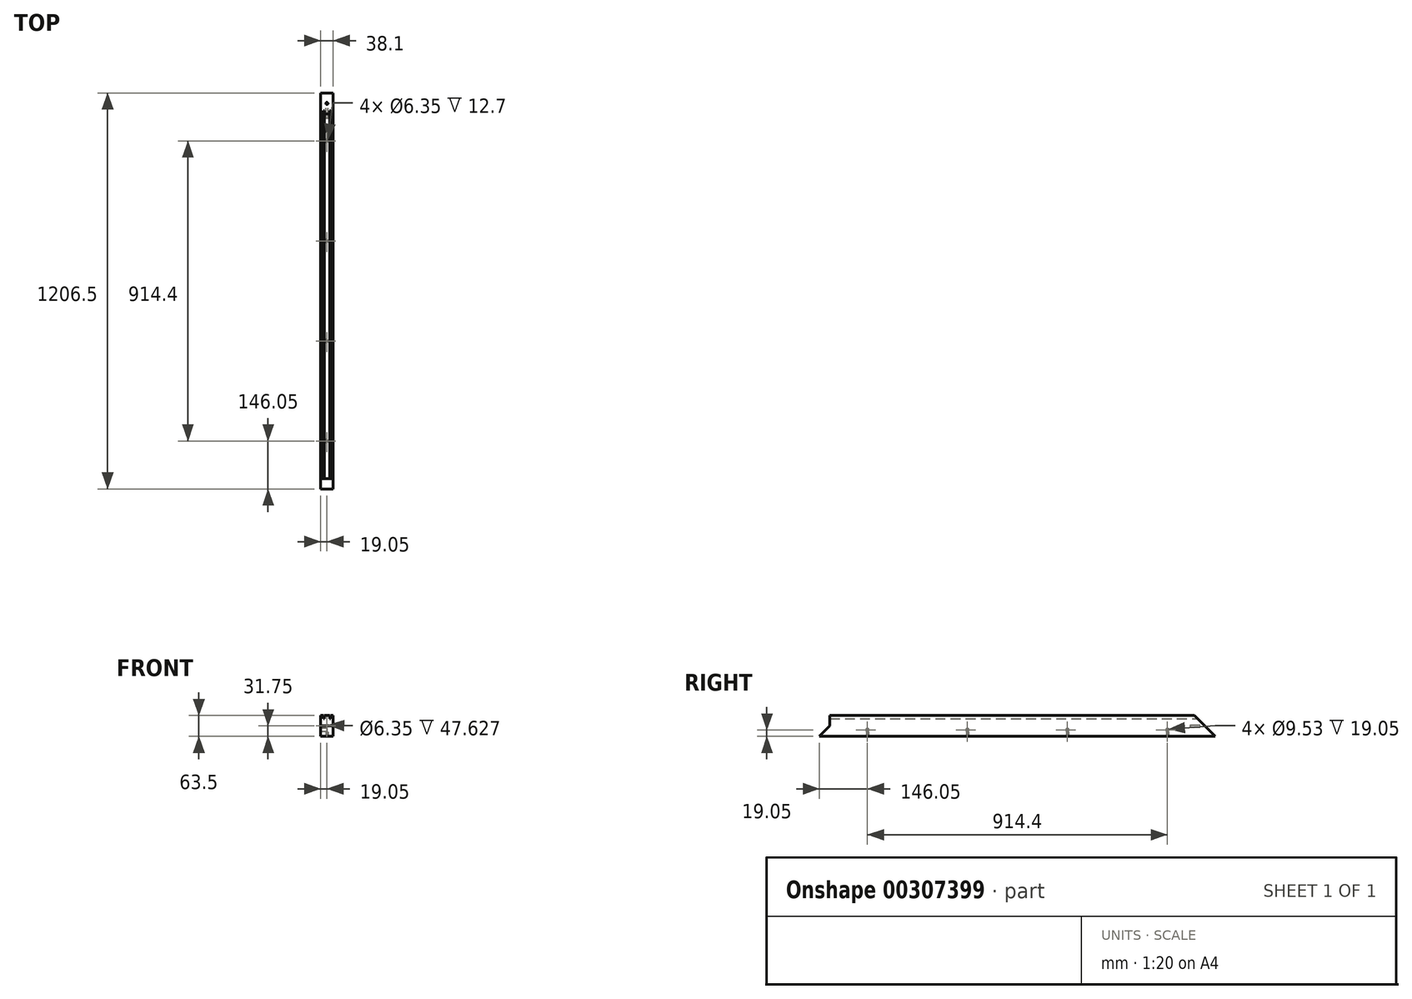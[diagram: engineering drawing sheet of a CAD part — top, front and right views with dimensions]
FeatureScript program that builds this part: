
annotation { "Feature Type Name" : "Feature", "Feature Type Description" : "" }
export const myFeature = defineFeature(function(context is Context, id is Id, definition is map)
    precondition{}
    {
        {
            var Q0;
            Q0=qCreatedBy(makeId("Front.planeOp"),FACE);
            var sketch = newSketch(context, id + "F0", { "sketchPlane" : qUnion([Q0])});
            skLineSegment(sketch, "E0.bottom", {"start": v(19.05, -31.75) * mm, "end": v(-19.05, -31.75) * mm});
            skLineSegment(sketch, "E0.top", {"start": v(19.05, 31.75) * mm, "end": v(-19.05, 31.75) * mm});
            skLineSegment(sketch, "E0.left", {"start": v(19.05, -31.75) * mm, "end": v(19.05, 31.75) * mm});
            skLineSegment(sketch, "E0.right", {"start": v(-19.05, -31.75) * mm, "end": v(-19.05, 31.75) * mm});
            skPoint(sketch, "E0.middle", {"position": v(0, 0) * mm});
            skLineSegment(sketch, "E1.bottom", {"start": v(11.11, 21.59) * mm, "end": v(7.94, 21.59) * mm});
            skLineSegment(sketch, "E1.top", {"start": v(11.11, 31.75) * mm, "end": v(7.94, 31.75) * mm});
            skLineSegment(sketch, "E1.left", {"start": v(11.11, 21.59) * mm, "end": v(11.11, 31.75) * mm});
            skLineSegment(sketch, "E1.right", {"start": v(7.94, 21.59) * mm, "end": v(7.94, 31.75) * mm});
            skPoint(sketch, "E1.middle", {"position": v(9.53, 26.67) * mm});
            skLineSegment(sketch, "E2.bottom", {"start": v(-7.94, 21.59) * mm, "end": v(-11.11, 21.59) * mm});
            skLineSegment(sketch, "E2.top", {"start": v(-7.94, 31.75) * mm, "end": v(-11.11, 31.75) * mm});
            skLineSegment(sketch, "E2.left", {"start": v(-7.94, 21.59) * mm, "end": v(-7.94, 31.75) * mm});
            skLineSegment(sketch, "E2.right", {"start": v(-11.11, 21.59) * mm, "end": v(-11.11, 31.75) * mm});
            skPoint(sketch, "E2.middle", {"position": v(-9.53, 26.67) * mm});
            skSolve(sketch);
        }
        {
            var Q0;
            Q0=makeQuery(id+"F0.imprint","IMPRINT",FACE,{"disambiguationData":[TD([[makeQuery(id+"F0.imprint","IMPRINT",EDGE,{"derivedFrom":sQuery(id+"F0.wireOp",EDGE,"E0.bottom")}),-1.0]])]});
            extrude(context, id + "F1", {"entities" : qUnion([Q0]), "endBound" : BoundingType.SYMMETRIC, "depth" : 1206.5 * mm});
        }
        {
            var Q0;
            Q0=qCreatedBy(makeId("Right.planeOp"),FACE);
            var sketch = newSketch(context, id + "F2", { "sketchPlane" : qUnion([Q0])});
            skLineSegment(sketch, "E3.MirrorCS", {"start": v(-571.5, 0) * mm, "end": v(-603.25, -31.75) * mm});
            skLineSegment(sketch, "E4.MirrorCS", {"start": v(-603.25, -31.75) * mm, "end": v(-603.25, 0) * mm});
            skLineSegment(sketch, "E5.MirrorCS", {"start": v(-571.5, 31.75) * mm, "end": v(-571.5, 0) * mm});
            skLineSegment(sketch, "E6.MirrorCS", {"start": v(-603.25, 31.75) * mm, "end": v(-603.25, 0) * mm});
            skLineSegment(sketch, "E7.MirrorCS", {"start": v(-603.25, 0) * mm, "end": v(-571.5, 0) * mm});
            skLineSegment(sketch, "E8.MirrorCS", {"start": v(-603.25, 31.75) * mm, "end": v(-571.5, 31.75) * mm});
            skPoint(sketch, "E9.MirrorP", {"position": v(-598.49, 4.76) * mm});
            skLineSegment(sketch, "E10", {"start": v(-571.5, 0) * mm, "end": v(-571.5, -31.75) * mm, "construction": true});
            skSolve(sketch);
        }
        {
            var Q0;
            Q0 = qSketchRegion(id + "F2", true);
            extrude(context, id + "F3", {"entities" : qUnion([Q0]), "operationType" : NewBodyOperationType.REMOVE, "endBound" : BoundingType.SYMMETRIC, "depth" : 127 * mm});
        }
        {
            var Q0;
            Q0=makeQuery(id+"F1.opExtrude","SWEPT_FACE",FACE,{"disambiguationData":[OSD([sQuery(id+"F0.wireOp",EDGE,"E0.right")])]});
            var sketch = newSketch(context, id + "F4", { "sketchPlane" : qUnion([Q0])});
            skLineSegment(sketch, "E11", {"start": v(-603.25, -31.75) * mm, "end": v(-539.75, 31.75) * mm});
            skLineSegment(sketch, "E12", {"start": v(-603.25, -31.75) * mm, "end": v(-603.25, 31.75) * mm});
            skLineSegment(sketch, "E13", {"start": v(-603.25, 31.75) * mm, "end": v(-539.75, 31.75) * mm});
            skSolve(sketch);
        }
        {
            var Q0;
            Q0=makeQuery(id+"F1.opExtrude","CAP_FACE",FACE,{"disambiguationData":[OSD([sQuery(id+"F0.wireOp",EDGE,"E0.bottom"),sQuery(id+"F0.wireOp",EDGE,"E0.top"),sQuery(id+"F0.wireOp",EDGE,"E0.left"),sQuery(id+"F0.wireOp",EDGE,"E0.right"),sQuery(id+"F0.wireOp",EDGE,"E1.bottom"),sQuery(id+"F0.wireOp",EDGE,"E1.left"),sQuery(id+"F0.wireOp",EDGE,"E1.right"),sQuery(id+"F0.wireOp",EDGE,"E2.bottom"),sQuery(id+"F0.wireOp",EDGE,"E2.left"),sQuery(id+"F0.wireOp",EDGE,"E2.right")])],"isStart":true});
            var sketch = newSketch(context, id + "F5", { "sketchPlane" : qUnion([Q0])});
            skCircle(sketch, "E14", {"center": v(0, 0) * mm, "radius": 3.18 * mm});
            skSolve(sketch);
        }
        {
            var Q0;
            Q0 = qSketchRegion(id + "F5", true);
            extrude(context, id + "F6", {"entities" : qUnion([Q0]), "operationType" : NewBodyOperationType.REMOVE, "oppositeDirection" : true, "depth" : 76.2 * mm});
        }
        {
            var Q0;
            Q0 = qSketchRegion(id + "F4", true);
            extrude(context, id + "F7", {"entities" : qUnion([Q0]), "operationType" : NewBodyOperationType.REMOVE, "oppositeDirection" : true, "depth" : 50.8 * mm});
        }
        {
            var Q0;
            Q0=makeQuery(id+"F1.opExtrude","SWEPT_FACE",FACE,{"disambiguationData":[OSD([sQuery(id+"F0.wireOp",EDGE,"E0.right")])]});
            var sketch = newSketch(context, id + "F8", { "sketchPlane" : qUnion([Q0])});
            skLineSegment(sketch, "E15.bottom", {"start": v(-603.25, -31.75) * mm, "end": v(603.25, -31.75) * mm, "construction": true});
            skLineSegment(sketch, "E15.top", {"start": v(-603.25, 6.35) * mm, "end": v(603.25, 6.35) * mm, "construction": true});
            skLineSegment(sketch, "E15.left", {"start": v(-603.25, -31.75) * mm, "end": v(-603.25, 6.35) * mm, "construction": true});
            skLineSegment(sketch, "E15.right", {"start": v(603.25, -31.75) * mm, "end": v(603.25, 6.35) * mm, "construction": true});
            skLineSegment(sketch, "E16", {"start": v(-603.25, -12.7) * mm, "end": v(603.25, -12.7) * mm, "construction": true});
            skPoint(sketch, "E17", {"position": v(0, -12.7) * mm});
            skPoint(sketch, "E18", {"position": v(-457.2, -12.7) * mm});
            skPoint(sketch, "E19", {"position": v(-152.4, -12.7) * mm});
            skPoint(sketch, "E20", {"position": v(152.4, -12.7) * mm});
            skPoint(sketch, "E21", {"position": v(457.2, -12.7) * mm});
            skLineSegment(sketch, "E22", {"start": v(0, -31.75) * mm, "end": v(0, 6.35) * mm, "construction": true});
            skPoint(sketch, "E22.startSnap0", {"position": v(0, -31.75) * mm});
            skCircle(sketch, "E23", {"center": v(-457.2, -12.7) * mm, "radius": 4.76 * mm});
            skCircle(sketch, "E24", {"center": v(-152.4, -12.7) * mm, "radius": 4.76 * mm});
            skCircle(sketch, "E25", {"center": v(152.4, -12.7) * mm, "radius": 4.76 * mm});
            skCircle(sketch, "E26", {"center": v(457.2, -12.7) * mm, "radius": 4.76 * mm});
            skSolve(sketch);
        }
        {
            var Q0;
            Q0 = qSketchRegion(id + "F8", true);
            extrude(context, id + "F9", {"entities" : qUnion([Q0]), "operationType" : NewBodyOperationType.REMOVE, "oppositeDirection" : true, "depth" : 19.05 * mm});
        }
        {
            var Q0;
            Q0=makeQuery(id+"F1.opExtrude","SWEPT_FACE",FACE,{"disambiguationData":[OSD([sQuery(id+"F0.wireOp",EDGE,"E0.bottom")])]});
            var sketch = newSketch(context, id + "F10", { "sketchPlane" : qUnion([Q0])});
            skCircle(sketch, "E27", {"center": v(0, -457.2) * mm, "radius": 3.18 * mm});
            skCircle(sketch, "E28", {"center": v(0, -152.4) * mm, "radius": 3.18 * mm});
            skCircle(sketch, "E29", {"center": v(0, 152.4) * mm, "radius": 3.18 * mm});
            skCircle(sketch, "E30", {"center": v(0, 457.2) * mm, "radius": 3.18 * mm});
            skSolve(sketch);
        }
        {
            var Q0;
            Q0 = qSketchRegion(id + "F10", true);
            extrude(context, id + "F11", {"entities" : qUnion([Q0]), "operationType" : NewBodyOperationType.REMOVE, "oppositeDirection" : true, "depth" : 12.7 * mm});
        }
    });
